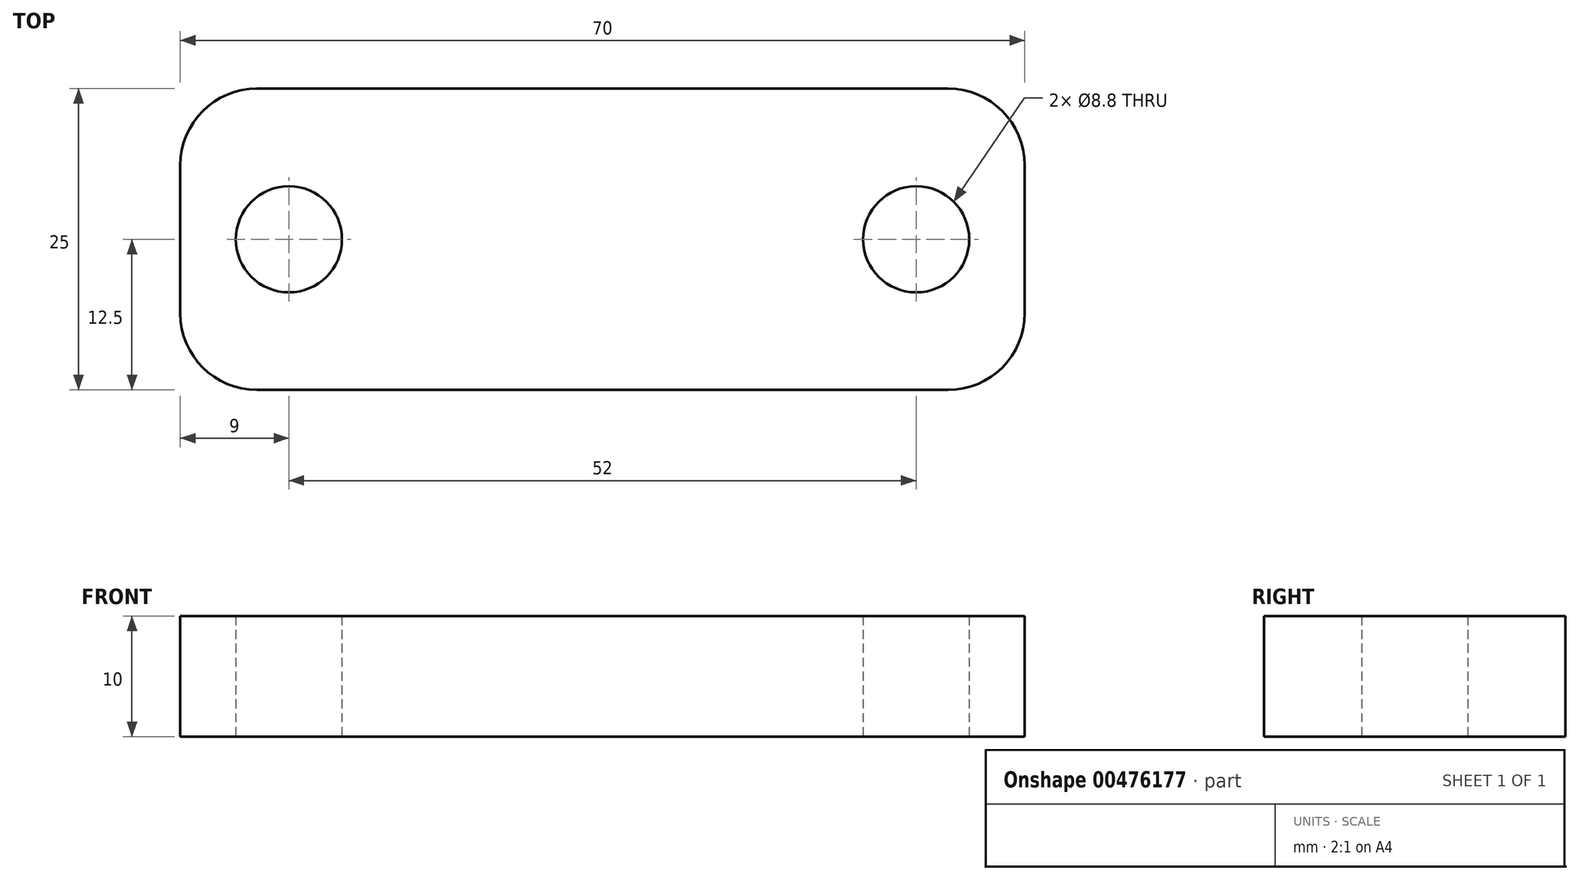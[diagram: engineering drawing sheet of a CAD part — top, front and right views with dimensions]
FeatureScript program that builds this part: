
annotation { "Feature Type Name" : "Feature", "Feature Type Description" : "" }
export const myFeature = defineFeature(function(context is Context, id is Id, definition is map)
    precondition{}
    {
        {
            var Q0;
            Q0=qCreatedBy(makeId("Top.planeOp"),FACE);
            var sketch = newSketch(context, id + "F0", { "sketchPlane" : qUnion([Q0])});
            skLineSegment(sketch, "E0.bottom", {"start": v(35, -12.5) * mm, "end": v(-35, -12.5) * mm});
            skLineSegment(sketch, "E0.top", {"start": v(35, 12.5) * mm, "end": v(-35, 12.5) * mm});
            skLineSegment(sketch, "E0.left", {"start": v(35, -12.5) * mm, "end": v(35, 12.5) * mm});
            skLineSegment(sketch, "E0.right", {"start": v(-35, -12.5) * mm, "end": v(-35, 12.5) * mm});
            skPoint(sketch, "E0.middle", {"position": v(0, 0) * mm});
            skCircle(sketch, "E1", {"center": v(-26, 0) * mm, "radius": 4.4 * mm});
            skCircle(sketch, "E2.MirrorC", {"center": v(26, 0) * mm, "radius": 4.4 * mm});
            skSolve(sketch);
        }
        {
            var Q0;
            Q0=makeQuery(id+"F0.imprint","IMPRINT",FACE,{"disambiguationData":[TD([[makeQuery(id+"F0.imprint","IMPRINT",EDGE,{"derivedFrom":sQuery(id+"F0.wireOp",EDGE,"E0.bottom")}),-1.0]])]});
            extrude(context, id + "F1", {"entities" : qUnion([Q0]), "depth" : 10 * mm});
        }
        {
            var Q0;
            Q0=makeQuery(id+"F1.opExtrude","SWEPT_EDGE",EDGE,{"disambiguationData":[OSD([sQuery(id+"F0.wireOp",EDGE,"E0.top"),sQuery(id+"F0.wireOp",EDGE,"E0.right")])]});
            var Q1;
            Q1=makeQuery(id+"F1.opExtrude","SWEPT_EDGE",EDGE,{"disambiguationData":[OSD([sQuery(id+"F0.wireOp",EDGE,"E0.top"),sQuery(id+"F0.wireOp",EDGE,"E0.left")])]});
            var Q2;
            Q2=makeQuery(id+"F1.opExtrude","SWEPT_EDGE",EDGE,{"disambiguationData":[OSD([sQuery(id+"F0.wireOp",EDGE,"E0.bottom"),sQuery(id+"F0.wireOp",EDGE,"E0.left")])]});
            var Q3;
            Q3=makeQuery(id+"F1.opExtrude","SWEPT_EDGE",EDGE,{"disambiguationData":[OSD([sQuery(id+"F0.wireOp",EDGE,"E0.bottom"),sQuery(id+"F0.wireOp",EDGE,"E0.right")])]});
            fillet(context, id + "F2", {"entities" : qUnion([Q0, Q1, Q2, Q3]), "radius" : 6.35 * mm, "tangentPropagation" : true, "allowEdgeOverflow" : false});
        }
    });
